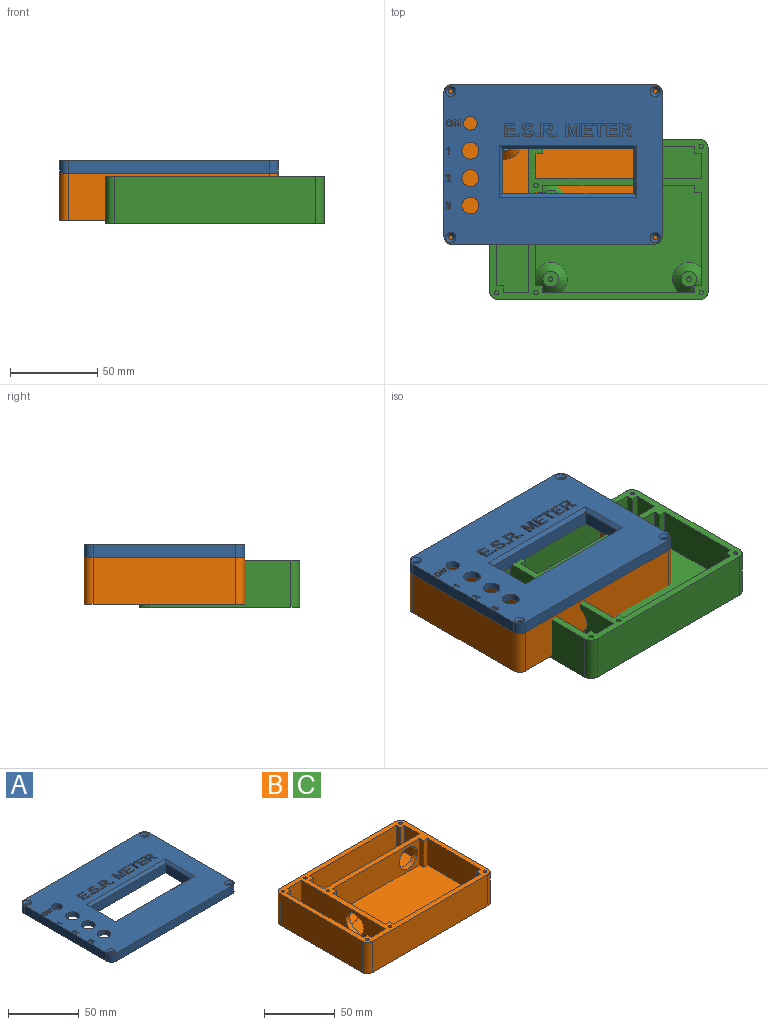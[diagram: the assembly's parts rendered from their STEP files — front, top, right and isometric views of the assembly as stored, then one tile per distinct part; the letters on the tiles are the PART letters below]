
ASSEMBLY  parts=3 mates=1
PART A: 312 faces, bbox 125.3x91.9x10 mm
  f0: plane 125.3x91.9mm, normal (0,0,1), area 8470.8mm2, adj f8,f9,f10,f11,f31,f32,f33,f34
  f1: plane 29.01x6mm, normal (-1,0,0), area 174.1mm2, adj f13,f43,f46,f47
  f2: plane 71.11x6mm, normal (0,1,0), area 426.7mm2, adj f13,f43,f44,f47
  f3: plane 71.44x6mm, normal (0,-1,0), area 428.6mm2, adj f13,f43,f45,f46
  f4: plane 27.36x6mm, normal (1,0,0), area 164.1mm2, adj f13,f43,f44,f45
  f5: plane 25.8x8mm, normal (1,0,0), area 206.4mm2, adj f6,f12,f42,f43
  f6: plane 74.8x8mm, normal (0,-1,0), area 598.4mm2, adj f5,f7,f40,f43
  f7: plane 25.8x8mm, normal (-1,0,0), area 206.4mm2, adj f6,f12,f39,f43
  f8: plane 81.9x7.1mm, normal (1,0,0), area 581.5mm2, adj f0,f26,f35,f38
  f9: plane 115.3x7.1mm, normal (0,1,0), area 818.6mm2, adj f0,f26,f35,f36
  f10: plane 81.9x7.1mm, normal (-1,0,0), area 581.5mm2, adj f0,f26,f36,f37
  f11: plane 115.3x7.1mm, normal (0,-1,0), area 818.6mm2, adj f0,f26,f37,f38
  f12: plane 74.8x8mm, normal (0,1,0), area 598.4mm2, adj f5,f7,f41,f43
  f13: plane 117.3x83.9mm, normal (0,0,-1), area 7111.6mm2, adj f1,f2,f3,f4,f14,f15,f16,f17
  f14: plane 4x3.1mm, normal (1,0,0), area 12.4mm2, adj f13,f15,f25,f26
  f15: plane 4x3.1mm, normal (0,-1,0), area 12.4mm2, adj f13,f14,f16,f26
  f16: plane 75.9x3.1mm, normal (1,0,0), area 235.3mm2, adj f13,f15,f17,f26
  f17: plane 4x3.1mm, normal (0,1,0), area 12.4mm2, adj f13,f16,f18,f26
  f18: plane 4x3.1mm, normal (1,0,0), area 12.4mm2, adj f13,f17,f19,f26
  f19: plane 109.3x3.1mm, normal (0,1,0), area 338.8mm2, adj f13,f18,f20,f26
  f20: plane 4x3.1mm, normal (-1,0,0), area 12.4mm2, adj f13,f19,f21,f26
  f21: plane 4x3.1mm, normal (0,1,0), area 12.4mm2, adj f13,f20,f22,f26
  f22: plane 75.9x3.1mm, normal (-1,0,0), area 235.3mm2, adj f13,f21,f23,f26
  f23: plane 4x3.1mm, normal (0,-1,0), area 12.4mm2, adj f13,f22,f24,f26
  f24: plane 4x3.1mm, normal (-1,0,0), area 12.4mm2, adj f13,f23,f25,f26
  f25: plane 109.3x3.1mm, normal (0,-1,0), area 338.8mm2, adj f13,f14,f24,f26
  f26: plane 125.3x91.9mm, normal (0,0,-1), area 1687.9mm2, adj f8,f9,f10,f11,f14,f15,f16,f17
  f27: cylinder r=1.5mm len=5.6mm, axis (0,0,1), area 52.8mm2, adj f26,f33
  f28: cylinder r=1.5mm len=5.6mm, axis (0,0,1), area 52.8mm2, adj f26,f32
  f29: cylinder r=1.5mm len=5.6mm, axis (0,0,1), area 52.8mm2, adj f26,f31
  f30: cylinder r=1.5mm len=5.6mm, axis (0,0,1), area 52.8mm2, adj f26,f34
  f31: cone r=1.5mm half-angle=45deg, axis (0,0,1), area 30mm2, adj f0,f29
  f32: cone r=1.5mm half-angle=45deg, axis (0,0,1), area 30mm2, adj f0,f28
  f33: cone r=1.5mm half-angle=45deg, axis (0,0,1), area 30mm2, adj f0,f27
  f34: cone r=1.5mm half-angle=45deg, axis (0,0,1), area 30mm2, adj f0,f30
  f35: cylinder r=5mm len=7.1mm, axis (0,0,1), area 55.8mm2, adj f0,f8,f9,f26
  f36: cylinder r=5mm len=7.1mm, axis (0,0,-1), area 55.8mm2, adj f0,f9,f10,f26
  f37: cylinder r=5mm len=7.1mm, axis (0,0,1), area 55.8mm2, adj f0,f10,f11,f26
  f38: cylinder r=5mm len=7.1mm, axis (0,0,-1), area 55.8mm2, adj f0,f8,f11,f26
  f39: plane 29.8x2mm, normal (-0.71,0,0.71), area 78.6mm2, adj f0,f7,f40,f41
  f40: plane 78.8x2mm, normal (0,-0.71,0.71), area 217.2mm2, adj f0,f6,f39,f42
  f41: plane 78.8x2mm, normal (0,0.71,0.71), area 217.2mm2, adj f0,f12,f39,f42
  f42: plane 29.8x2mm, normal (0.71,0,0.71), area 78.6mm2, adj f0,f5,f40,f41
  f43: plane 80.2x35.88mm, normal (0,0,-1), area 445.3mm2, adj f1,f2,f3,f4,f5,f6,f7,f12
  f44: cylinder r=2.3mm len=6mm, axis (0,0,1), area 60.5mm2, adj f2,f4,f13,f43
  f45: cylinder r=2.3mm len=6mm, axis (0,0,1), area 63.5mm2, adj f3,f4,f13,f43
  f46: cylinder r=2.3mm len=6mm, axis (0,0,1), area 56.6mm2, adj f1,f3,f13,f43
  f47: cylinder r=2.3mm len=6mm, axis (0,0,1), area 53.5mm2, adj f1,f2,f13,f43
  f48: cylinder r=1.3mm len=8mm, axis (0,0,-1), area 65.3mm2, adj f43,f49
  f49: plane 2.6x2.6mm, normal (0,0,-1), area 5.3mm2, adj f48
  f50: cylinder r=1.3mm len=8mm, axis (0,0,-1), area 65.3mm2, adj f43,f51
  f51: plane 2.6x2.6mm, normal (0,0,-1), area 5.3mm2, adj f50
  f52: cylinder r=1.3mm len=8mm, axis (0,0,-1), area 65.3mm2, adj f43,f53
  f53: plane 2.6x2.6mm, normal (0,0,-1), area 5.3mm2, adj f52
  f54: cylinder r=1.3mm len=8mm, axis (0,0,-1), area 65.3mm2, adj f43,f55
  f55: plane 2.6x2.6mm, normal (0,0,-1), area 5.3mm2, adj f54
  f56: cylinder r=4.85mm len=9.7mm, axis (0,0,1), area 121.9mm2, adj f0,f13
  f57: cylinder r=4.85mm len=9.7mm, axis (0,0,1), area 121.9mm2, adj f0,f13
  f58: cylinder r=4.85mm len=9.7mm, axis (0,0,1), area 121.9mm2, adj f0,f13
  f59: cylinder r=3.9mm len=7.8mm, axis (0,0,1), area 98mm2, adj f0,f13
  f60: plane 2x1.65mm, normal (-1,0,0), area 3.3mm2, adj f0,f61,f63,f64
  f61: plane 2x1.57mm, normal (0,-1,0), area 3.1mm2, adj f0,f60,f62,f64
  f62: plane 2x1.65mm, normal (1,0,0), area 3.3mm2, adj f0,f61,f63,f64
  f63: plane 2x1.57mm, normal (0,1,0), area 3.1mm2, adj f0,f60,f62,f64
  f64: plane 1.65x1.57mm, normal (0,0,1), area 2.6mm2, adj f60,f61,f62,f63
  f65: extruded ~2x1.02mm, area 2.2mm2, adj f66,f81,f83,f84
  f66: plane 2.09x2mm, normal (0,-1,0), area 4.2mm2, adj f65,f67,f83,f84
  f67: plane 2.26x2mm, normal (-1,0,0), area 4.5mm2, adj f66,f68,f83,f84
  f68: plane 2.05x2mm, normal (0,1,0), area 4.1mm2, adj f67,f69,f83,f84
  f69: extruded ~2x1.41mm, area 4.1mm2, adj f68,f81,f83,f84
  f70: plane 3.21x2.07mm, normal (-0.84,-0.54,0), area 7.6mm2, adj f0,f71,f82,f83
  f71: extruded ~2x1.23mm, area 3mm2, adj f0,f70,f72,f83
  f72: extruded ~2x1.39mm, area 3mm2, adj f0,f71,f73,f83
  f73: extruded ~2x1.69mm, area 3.8mm2, adj f0,f72,f74,f83
  f74: extruded ~2.11x2mm, area 4.5mm2, adj f0,f73,f75,f83
  f75: plane 3.82x2mm, normal (0,-1,0), area 7.6mm2, adj f0,f74,f76,f83
  f76: plane 7.64x2mm, normal (1,0,0), area 15.3mm2, adj f0,f75,f77,f83
  f77: plane 2x1.6mm, normal (0,1,0), area 3.2mm2, adj f0,f76,f78,f83
  f78: plane 2.9x2mm, normal (-1,0,0), area 5.8mm2, adj f0,f77,f79,f83
  f79: plane 2x1.88mm, normal (0,1,0), area 3.8mm2, adj f0,f78,f80,f83
  f80: plane 2.9x2mm, normal (0.85,0.52,0), area 6.8mm2, adj f0,f79,f82,f83
  f81: extruded ~2x0.85mm, area 1.9mm2, adj f65,f69,f83,f84
  f82: plane 2x1.8mm, normal (0,1,0), area 3.6mm2, adj f0,f70,f80,f83
  f83: plane 7.64x7.05mm, normal (0,0,1), area 31.6mm2, adj f65,f66,f67,f68,f69,f70,f71,f72
  f84: plane 3.46x2.26mm, normal (0,0,1), area 7.3mm2, adj f65,f66,f67,f68,f69,f81
  f85: extruded ~2x0.76mm, area 1.7mm2, adj f86,f97,f99,f100
  f86: extruded ~2x1.34mm, area 3.8mm2, adj f85,f87,f99,f100
  f87: extruded ~2x1.34mm, area 3.8mm2, adj f86,f88,f99,f100
  f88: extruded ~2x0.75mm, area 1.7mm2, adj f87,f89,f99,f100
  f89: extruded ~2x1mm, area 2.1mm2, adj f88,f97,f99,f100
  f90: extruded ~2x1.4mm, area 3.1mm2, adj f0,f91,f98,f99
  f91: extruded ~2x1.4mm, area 3.1mm2, adj f0,f90,f92,f99
  f92: extruded ~2x1.51mm, area 3.3mm2, adj f0,f91,f93,f99
  f93: extruded ~2x1.52mm, area 3.3mm2, adj f0,f92,f94,f99
  f94: extruded ~2x1.4mm, area 3.1mm2, adj f0,f93,f95,f99
  f95: extruded ~2x1.4mm, area 3.1mm2, adj f0,f94,f96,f99
  f96: extruded ~2x1.51mm, area 3.3mm2, adj f0,f95,f98,f99
  f97: extruded ~2x1mm, area 2.1mm2, adj f85,f89,f99,f100
  f98: extruded ~2x1.51mm, area 3.3mm2, adj f0,f90,f96,f99
  f99: plane 4.08x3.78mm, normal (0,0,1), area 8.2mm2, adj f85,f86,f87,f88,f89,f90,f91,f92
  f100: plane 2.68x2.01mm, normal (0,0,1), area 4.5mm2, adj f85,f86,f87,f88,f89,f97
  f101: plane 2x1.24mm, normal (-1,0,0), area 2.5mm2, adj f0,f102,f112,f113
  f102: plane 4.63x2mm, normal (0,-1,0), area 9.3mm2, adj f0,f101,f103,f113
  f103: plane 2.01x2mm, normal (-1,0,0), area 4mm2, adj f0,f102,f104,f113
  f104: plane 4.08x2mm, normal (0,1,0), area 8.2mm2, adj f0,f103,f105,f113
  f105: plane 2x1.24mm, normal (-1,0,0), area 2.5mm2, adj f0,f104,f106,f113
  f106: plane 4.08x2mm, normal (0,-1,0), area 8.2mm2, adj f0,f105,f107,f113
  f107: plane 2x1.92mm, normal (-1,0,0), area 3.8mm2, adj f0,f106,f108,f113
  f108: plane 4.41x2mm, normal (0,1,0), area 8.8mm2, adj f0,f107,f109,f113
  f109: plane 2x1.24mm, normal (-1,0,0), area 2.5mm2, adj f0,f108,f110,f113
  f110: plane 6.01x2mm, normal (0,-1,0), area 12mm2, adj f0,f109,f111,f113
  f111: plane 7.64x2mm, normal (1,0,0), area 15.3mm2, adj f0,f110,f112,f113
  f112: plane 6.23x2mm, normal (0,1,0), area 12.5mm2, adj f0,f101,f111,f113
  f113: plane 7.64x6.23mm, normal (0,0,1), area 28.5mm2, adj f101,f102,f103,f104,f105,f106,f107,f108
  f114: plane 2x1.24mm, normal (-1,0,0), area 2.5mm2, adj f0,f115,f125,f126
  f115: plane 4.63x2mm, normal (0,-1,0), area 9.3mm2, adj f0,f114,f116,f126
  f116: plane 2.01x2mm, normal (-1,0,0), area 4mm2, adj f0,f115,f117,f126
  f117: plane 4.08x2mm, normal (0,1,0), area 8.2mm2, adj f0,f116,f118,f126
  f118: plane 2x1.24mm, normal (-1,0,0), area 2.5mm2, adj f0,f117,f119,f126
  f119: plane 4.08x2mm, normal (0,-1,0), area 8.2mm2, adj f0,f118,f120,f126
  f120: plane 2x1.92mm, normal (-1,0,0), area 3.8mm2, adj f0,f119,f121,f126
  f121: plane 4.41x2mm, normal (0,1,0), area 8.8mm2, adj f0,f120,f122,f126
  f122: plane 2x1.24mm, normal (-1,0,0), area 2.5mm2, adj f0,f121,f123,f126
  f123: plane 6.01x2mm, normal (0,-1,0), area 12mm2, adj f0,f122,f124,f126
  f124: plane 7.64x2mm, normal (1,0,0), area 15.3mm2, adj f0,f123,f125,f126
  f125: plane 6.23x2mm, normal (0,1,0), area 12.5mm2, adj f0,f114,f124,f126
  f126: plane 7.64x6.23mm, normal (0,0,1), area 28.5mm2, adj f114,f115,f116,f117,f118,f119,f120,f121
  f127: plane 2x1.24mm, normal (-1,0,0), area 2.5mm2, adj f0,f128,f134,f135
  f128: plane 6.54x2mm, normal (0,-1,0), area 13.1mm2, adj f0,f127,f129,f135
  f129: plane 2x1.24mm, normal (1,0,0), area 2.5mm2, adj f0,f128,f130,f135
  f130: plane 2.47x2mm, normal (0,1,0), area 4.9mm2, adj f0,f129,f131,f135
  f131: plane 6.41x2mm, normal (1,0,0), area 12.8mm2, adj f0,f130,f132,f135
  f132: plane 2x1.6mm, normal (0,1,0), area 3.2mm2, adj f0,f131,f133,f135
  f133: plane 6.41x2mm, normal (-1,0,0), area 12.8mm2, adj f0,f132,f134,f135
  f134: plane 2.47x2mm, normal (0,1,0), area 4.9mm2, adj f0,f127,f133,f135
  f135: plane 7.64x6.54mm, normal (0,0,1), area 18.3mm2, adj f127,f128,f129,f130,f131,f132,f133,f134
  f136: plane 2x1.24mm, normal (-1,0,0), area 2.5mm2, adj f0,f137,f147,f148
  f137: plane 4.63x2mm, normal (0,-1,0), area 9.3mm2, adj f0,f136,f138,f148
  f138: plane 2.01x2mm, normal (-1,0,0), area 4mm2, adj f0,f137,f139,f148
  f139: plane 4.08x2mm, normal (0,1,0), area 8.2mm2, adj f0,f138,f140,f148
  f140: plane 2x1.24mm, normal (-1,0,0), area 2.5mm2, adj f0,f139,f141,f148
  f141: plane 4.08x2mm, normal (0,-1,0), area 8.2mm2, adj f0,f140,f142,f148
  f142: plane 2x1.92mm, normal (-1,0,0), area 3.8mm2, adj f0,f141,f143,f148
  f143: plane 4.41x2mm, normal (0,1,0), area 8.8mm2, adj f0,f142,f144,f148
  f144: plane 2x1.24mm, normal (-1,0,0), area 2.5mm2, adj f0,f143,f145,f148
  f145: plane 6.01x2mm, normal (0,-1,0), area 12mm2, adj f0,f144,f146,f148
  f146: plane 7.64x2mm, normal (1,0,0), area 15.3mm2, adj f0,f145,f147,f148
  f147: plane 6.23x2mm, normal (0,1,0), area 12.5mm2, adj f0,f136,f146,f148
  f148: plane 7.64x6.23mm, normal (0,0,1), area 28.5mm2, adj f136,f137,f138,f139,f140,f141,f142,f143
  f149: plane 2x0.76mm, normal (0,-1,0), area 1.5mm2, adj f0,f150,f162,f163
  f150: plane 2x1.88mm, normal (1,0,0), area 3.8mm2, adj f0,f149,f151,f163
  f151: extruded ~2x1.09mm, area 2.2mm2, adj f0,f150,f152,f163
  f152: plane 2x0.02mm, normal (0,-1,0), area 0mm2, adj f0,f151,f153,f163
  f153: plane 2.97x2mm, normal (-0.87,-0.5,0), area 6.9mm2, adj f0,f152,f154,f163
  f154: plane 2x1.06mm, normal (0,-1,0), area 2.1mm2, adj f0,f153,f155,f163
  f155: plane 3.97x2mm, normal (1,0,0), area 7.9mm2, adj f0,f154,f156,f163
  f156: plane 2x0.75mm, normal (0,1,0), area 1.5mm2, adj f0,f155,f157,f163
  f157: plane 2x1.87mm, normal (-1,0,0), area 3.7mm2, adj f0,f156,f158,f163
  f158: extruded ~2x1.13mm, area 2.3mm2, adj f0,f157,f159,f163
  f159: plane 2x0.02mm, normal (0,1,0), area 0mm2, adj f0,f158,f160,f163
  f160: plane 3x2mm, normal (0.87,0.5,0), area 6.9mm2, adj f0,f159,f161,f163
  f161: plane 2x1.07mm, normal (0,1,0), area 2.1mm2, adj f0,f160,f162,f163
  f162: plane 3.97x2mm, normal (-1,0,0), area 7.9mm2, adj f0,f149,f161,f163
  f163: plane 3.97x3.52mm, normal (0,0,1), area 8.9mm2, adj f149,f150,f151,f152,f153,f154,f155,f156
  f164: plane 7.64x2mm, normal (-1,0,0), area 15.3mm2, adj f0,f165,f184,f185
  f165: plane 2.13x2mm, normal (0,-1,0), area 4.3mm2, adj f0,f164,f166,f185
  f166: plane 4.49x2mm, normal (0.95,-0.3,0), area 9.4mm2, adj f0,f165,f167,f185
  f167: plane 2x1.23mm, normal (0.96,-0.27,0), area 2.5mm2, adj f0,f166,f168,f185
  f168: plane 2x1.02mm, normal (-0.97,-0.25,0), area 2.1mm2, adj f0,f167,f169,f185
  f169: plane 2x0.41mm, normal (-0.96,-0.28,0), area 0.9mm2, adj f0,f168,f170,f185
  f170: plane 4.27x2mm, normal (-0.95,-0.3,0), area 9mm2, adj f0,f169,f171,f185
  f171: plane 2.14x2mm, normal (0,-1,0), area 4.3mm2, adj f0,f170,f172,f185
  f172: plane 7.64x2mm, normal (1,0,0), area 15.3mm2, adj f0,f171,f173,f185
  f173: plane 2x1.42mm, normal (0,1,0), area 2.8mm2, adj f0,f172,f174,f185
  f174: plane 4.63x2mm, normal (-1,0,0), area 9.3mm2, adj f0,f173,f175,f185
  f175: extruded ~2x1.67mm, area 3.3mm2, adj f0,f174,f176,f185
  f176: plane 2.03x2mm, normal (0.96,0.27,0), area 4.2mm2, adj f0,f175,f177,f185
  f177: plane 4.26x2mm, normal (0.95,0.31,0), area 9mm2, adj f0,f176,f178,f185
  f178: plane 2x1.14mm, normal (0,1,0), area 2.3mm2, adj f0,f177,f179,f185
  f179: plane 4.26x2mm, normal (-0.95,0.31,0), area 9mm2, adj f0,f178,f180,f185
  f180: extruded ~2.03x2mm, area 4.2mm2, adj f0,f179,f181,f185
  f181: extruded ~2x1.35mm, area 2.7mm2, adj f0,f180,f182,f185
  f182: extruded ~2x0.31mm, area 0.6mm2, adj f0,f181,f183,f185
  f183: plane 4.63x2mm, normal (1,0,0), area 9.3mm2, adj f0,f182,f184,f185
  f184: plane 2x1.42mm, normal (0,1,0), area 2.8mm2, adj f0,f164,f183,f185
  f185: plane 7.77x7.64mm, normal (0,0,1), area 38.4mm2, adj f164,f165,f166,f167,f168,f169,f170,f171
  f186: plane 2x1.65mm, normal (-1,0,0), area 3.3mm2, adj f0,f187,f189,f190
  f187: plane 2x1.57mm, normal (0,-1,0), area 3.1mm2, adj f0,f186,f188,f190
  f188: plane 2x1.65mm, normal (1,0,0), area 3.3mm2, adj f0,f187,f189,f190
  f189: plane 2x1.57mm, normal (0,1,0), area 3.1mm2, adj f0,f186,f188,f190
  f190: plane 1.65x1.57mm, normal (0,0,1), area 2.6mm2, adj f186,f187,f188,f189
  f191: plane 2x1.65mm, normal (-1,0,0), area 3.3mm2, adj f0,f192,f194,f195
  f192: plane 2x1.57mm, normal (0,-1,0), area 3.1mm2, adj f0,f191,f193,f195
  f193: plane 2x1.65mm, normal (1,0,0), area 3.3mm2, adj f0,f192,f194,f195
  f194: plane 2x1.57mm, normal (0,1,0), area 3.1mm2, adj f0,f191,f193,f195
  f195: plane 1.65x1.57mm, normal (0,0,1), area 2.6mm2, adj f191,f192,f193,f194
  f196: extruded ~2x0.63mm, area 1.5mm2, adj f0,f197,f226,f227
  f197: extruded ~2x0.75mm, area 1.8mm2, adj f0,f196,f198,f227
  f198: extruded ~2x1.58mm, area 3.3mm2, adj f0,f197,f199,f227
  f199: extruded ~2x1.23mm, area 2.6mm2, adj f0,f198,f200,f227
  f200: extruded ~2x0.46mm, area 1.1mm2, adj f0,f199,f201,f227
  f201: extruded ~2x0.49mm, area 1mm2, adj f0,f200,f202,f227
  f202: extruded ~2x1.45mm, area 3.9mm2, adj f0,f201,f203,f227
  f203: extruded ~2x1.05mm, area 2.2mm2, adj f0,f202,f204,f227
  f204: extruded ~2x0.74mm, area 1.8mm2, adj f0,f203,f205,f227
  f205: plane 2x1.55mm, normal (-0.14,0.99,0), area 3.1mm2, adj f0,f204,f206,f227
  f206: extruded ~2x1.47mm, area 3.6mm2, adj f0,f205,f207,f227
  f207: extruded ~2.13x2mm, area 4.4mm2, adj f0,f206,f208,f227
  f208: extruded ~2.26x2mm, area 4.7mm2, adj f0,f207,f209,f227
  f209: extruded ~2x1.59mm, area 3.7mm2, adj f0,f208,f210,f227
  f210: extruded ~2x0.72mm, area 1.5mm2, adj f0,f209,f211,f227
  f211: extruded ~2x0.55mm, area 1.3mm2, adj f0,f210,f212,f227
  f212: extruded ~2x0.46mm, area 1.2mm2, adj f0,f211,f213,f227
  f213: extruded ~2x0.61mm, area 1.3mm2, adj f0,f212,f214,f227
  f214: extruded ~2x1.19mm, area 2.5mm2, adj f0,f213,f215,f227
  f215: extruded ~2x1.34mm, area 2.8mm2, adj f0,f214,f216,f227
  f216: extruded ~2x0.54mm, area 1.3mm2, adj f0,f215,f217,f227
  f217: extruded ~2x0.54mm, area 1.2mm2, adj f0,f216,f218,f227
  f218: extruded ~2x1.68mm, area 4.4mm2, adj f0,f217,f219,f227
  f219: extruded ~2x1.26mm, area 2.6mm2, adj f0,f218,f220,f227
  f220: extruded ~2x0.88mm, area 2.2mm2, adj f0,f219,f221,f227
  f221: plane 2x1.55mm, normal (0.16,-0.99,0), area 3.1mm2, adj f0,f220,f222,f227
  f222: extruded ~2x1.58mm, area 3.9mm2, adj f0,f221,f223,f227
  f223: extruded ~2.31x2mm, area 4.8mm2, adj f0,f222,f224,f227
  f224: extruded ~2.44x2mm, area 5.1mm2, adj f0,f223,f225,f227
  f225: extruded ~2x1.72mm, area 4mm2, adj f0,f224,f226,f227
  f226: extruded ~2x0.84mm, area 1.7mm2, adj f0,f196,f225,f227
  f227: plane 7.87x6.66mm, normal (0,0,1), area 26.8mm2, adj f196,f197,f198,f199,f200,f201,f202,f203
  f228: extruded ~2x1.02mm, area 2.2mm2, adj f229,f244,f246,f247
  f229: plane 2.09x2mm, normal (0,-1,0), area 4.2mm2, adj f228,f230,f246,f247
  f230: plane 2.26x2mm, normal (-1,0,0), area 4.5mm2, adj f229,f231,f246,f247
  f231: plane 2.05x2mm, normal (0,1,0), area 4.1mm2, adj f230,f232,f246,f247
  f232: extruded ~2x1.41mm, area 4.1mm2, adj f231,f244,f246,f247
  f233: plane 3.21x2.07mm, normal (-0.84,-0.54,0), area 7.6mm2, adj f0,f234,f245,f246
  f234: extruded ~2x1.23mm, area 3mm2, adj f0,f233,f235,f246
  f235: extruded ~2x1.39mm, area 3mm2, adj f0,f234,f236,f246
  f236: extruded ~2x1.69mm, area 3.8mm2, adj f0,f235,f237,f246
  f237: extruded ~2.11x2mm, area 4.5mm2, adj f0,f236,f238,f246
  f238: plane 3.82x2mm, normal (0,-1,0), area 7.6mm2, adj f0,f237,f239,f246
  f239: plane 7.64x2mm, normal (1,0,0), area 15.3mm2, adj f0,f238,f240,f246
  f240: plane 2x1.6mm, normal (0,1,0), area 3.2mm2, adj f0,f239,f241,f246
  f241: plane 2.9x2mm, normal (-1,0,0), area 5.8mm2, adj f0,f240,f242,f246
  f242: plane 2x1.88mm, normal (0,1,0), area 3.8mm2, adj f0,f241,f243,f246
  f243: plane 2.9x2mm, normal (0.85,0.52,0), area 6.8mm2, adj f0,f242,f245,f246
  f244: extruded ~2x0.85mm, area 1.9mm2, adj f228,f232,f246,f247
  f245: plane 2x1.8mm, normal (0,1,0), area 3.6mm2, adj f0,f233,f243,f246
  f246: plane 7.64x7.05mm, normal (0,0,1), area 31.6mm2, adj f228,f229,f230,f231,f232,f233,f234,f235
  f247: plane 3.46x2.26mm, normal (0,0,1), area 7.3mm2, adj f228,f229,f230,f231,f232,f244
  f248: plane 2x0.69mm, normal (0,-1,0), area 1.4mm2, adj f0,f249,f257,f258
  f249: plane 2x1.28mm, normal (0.62,-0.78,0), area 3.3mm2, adj f0,f248,f250,f258
  f250: plane 2x0.5mm, normal (0.78,0.63,0), area 1.3mm2, adj f0,f249,f251,f258
  f251: plane 2x0.46mm, normal (-0.63,0.78,0), area 1.2mm2, adj f0,f250,f252,f258
  f252: extruded ~2x0.29mm, area 0.8mm2, adj f0,f251,f253,f258
  f253: plane 2x0.41mm, normal (1,-0.03,0), area 0.8mm2, adj f0,f252,f254,f258
  f254: plane 2x0.38mm, normal (1,-0.02,0), area 0.8mm2, adj f0,f253,f255,f258
  f255: plane 2.3x2mm, normal (1,0,0), area 4.6mm2, adj f0,f254,f256,f258
  f256: plane 2x0.84mm, normal (0,1,0), area 1.7mm2, adj f0,f255,f257,f258
  f257: plane 3.97x2mm, normal (-1,0,0), area 7.9mm2, adj f0,f248,f256,f258
  f258: plane 3.97x1.97mm, normal (0,0,1), area 4.1mm2, adj f248,f249,f250,f251,f252,f253,f254,f255
  f259: plane 2x1.73mm, normal (0,-1,0), area 3.5mm2, adj f0,f260,f282,f283
  f260: plane 2x0.04mm, normal (-1,0,0), area 0.1mm2, adj f0,f259,f261,f283
  f261: plane 2x0.51mm, normal (-0.69,0.73,0), area 1.4mm2, adj f0,f260,f262,f283
  f262: extruded ~2x0.72mm, area 2mm2, adj f0,f261,f263,f283
  f263: extruded ~2x0.49mm, area 1.2mm2, adj f0,f262,f264,f283
  f264: extruded ~2x0.51mm, area 1.1mm2, adj f0,f263,f265,f283
  f265: extruded ~2x0.56mm, area 1.2mm2, adj f0,f264,f266,f283
  f266: extruded ~2x0.44mm, area 1.2mm2, adj f0,f265,f267,f283
  f267: extruded ~2x0.66mm, area 1.4mm2, adj f0,f266,f268,f283
  f268: extruded ~2x0.51mm, area 1mm2, adj f0,f267,f269,f283
  f269: extruded ~2x0.42mm, area 0.9mm2, adj f0,f268,f270,f283
  f270: extruded ~2x0.49mm, area 1.2mm2, adj f0,f269,f271,f283
  f271: plane 2x0.54mm, normal (0.76,0.65,0), area 1.4mm2, adj f0,f270,f272,f283
  f272: extruded ~2x0.45mm, area 1.1mm2, adj f0,f271,f273,f283
  f273: extruded ~2x0.45mm, area 0.9mm2, adj f0,f272,f274,f283
  f274: extruded ~2x0.35mm, area 0.8mm2, adj f0,f273,f275,f283
  f275: extruded ~2x0.36mm, area 0.8mm2, adj f0,f274,f276,f283
  f276: extruded ~2x0.31mm, area 0.6mm2, adj f0,f275,f277,f283
  f277: extruded ~2x0.32mm, area 0.8mm2, adj f0,f276,f278,f283
  f278: extruded ~2x0.63mm, area 1.7mm2, adj f0,f277,f279,f283
  f279: plane 2x1.01mm, normal (0.71,-0.7,0), area 2.8mm2, adj f0,f278,f280,f283
  f280: plane 2x0.58mm, normal (1,0,0), area 1.2mm2, adj f0,f279,f281,f283
  f281: plane 2.77x2mm, normal (0,1,0), area 5.5mm2, adj f0,f280,f282,f283
  f282: plane 2x0.71mm, normal (-1,0,0), area 1.4mm2, adj f0,f259,f281,f283
  f283: plane 4.02x2.78mm, normal (0,0,1), area 5.9mm2, adj f259,f260,f261,f262,f263,f264,f265,f266
  f284: extruded ~2x0.97mm, area 2mm2, adj f0,f285,f310,f311
  f285: extruded ~2x1.29mm, area 2.7mm2, adj f0,f284,f286,f311
  f286: plane 2x0.58mm, normal (0.83,0.56,0), area 1.4mm2, adj f0,f285,f287,f311
  f287: extruded ~2x0.45mm, area 1mm2, adj f0,f286,f288,f311
  f288: extruded ~2x0.4mm, area 0.8mm2, adj f0,f287,f289,f311
  f289: extruded ~2x0.56mm, area 1.7mm2, adj f0,f288,f290,f311
  f290: extruded ~2x0.41mm, area 1mm2, adj f0,f289,f291,f311
  f291: extruded ~2x0.67mm, area 1.4mm2, adj f0,f290,f292,f311
  f292: plane 2x0.31mm, normal (0,-1,0), area 0.6mm2, adj f0,f291,f293,f311
  f293: plane 2x0.64mm, normal (1,0,0), area 1.3mm2, adj f0,f292,f294,f311
  f294: plane 2x0.3mm, normal (0,1,0), area 0.6mm2, adj f0,f293,f295,f311
  f295: extruded ~2x0.73mm, area 1.5mm2, adj f0,f294,f296,f311
  f296: extruded ~2x0.4mm, area 1mm2, adj f0,f295,f297,f311
  f297: extruded ~2x0.45mm, area 1mm2, adj f0,f296,f298,f311
  f298: extruded ~2x0.61mm, area 1.3mm2, adj f0,f297,f299,f311
  f299: extruded ~2x0.55mm, area 1.1mm2, adj f0,f298,f300,f311
  f300: extruded ~2x0.51mm, area 1.1mm2, adj f0,f299,f301,f311
  f301: plane 2x0.71mm, normal (1,0,0), area 1.4mm2, adj f0,f300,f302,f311
  f302: extruded ~2x1.15mm, area 2.3mm2, adj f0,f301,f303,f311
  f303: extruded ~2x1.19mm, area 2.5mm2, adj f0,f302,f304,f311
  f304: extruded ~2x0.89mm, area 2mm2, adj f0,f303,f305,f311
  f305: extruded ~2x0.63mm, area 1.4mm2, adj f0,f304,f306,f311
  f306: extruded ~2x0.73mm, area 1.6mm2, adj f0,f305,f307,f311
  f307: plane 2x0.02mm, normal (-1,0,0), area 0mm2, adj f0,f306,f308,f311
  f308: extruded ~2x0.63mm, area 1.5mm2, adj f0,f307,f309,f311
  f309: extruded ~2x0.63mm, area 1.4mm2, adj f0,f308,f310,f311
  f310: extruded ~2x0.69mm, area 1.6mm2, adj f0,f284,f309,f311
  f311: plane 4.08x2.74mm, normal (0,0,1), area 5.9mm2, adj f284,f285,f286,f287,f288,f289,f290,f291
PART B: 72 faces, bbox 125.9x92.5x27.6 mm
  f0: plane 94.8x23mm, normal (0,1,0), area 1925.9mm2, adj f17,f32,f34,f35,f40
  f1: plane 83.9x23mm, normal (-1,0,0), area 1675.2mm2, adj f17,f41,f43,f49,f54
  f2: plane 115.3x27mm, normal (0,-1,0), area 3113.1mm2, adj f4,f17,f51,f53
  f3: plane 81.9x27mm, normal (1,0,0), area 2211.3mm2, adj f4,f17,f52,f53
  f4: plane 125.3x91.9mm, normal (0,0,-1), area 11493.6mm2, adj f2,f3,f31,f42,f50,f51,f52,f53
  f5: plane 23x4mm, normal (0,-1,0), area 92mm2, adj f6,f16,f17,f18
  f6: plane 53.6x23mm, normal (-1,0,0), area 1214.2mm2, adj f5,f7,f17,f18,f69
  f7: plane 21.47x4mm, normal (0,1,0), area 79.3mm2, adj f6,f8,f17,f69
  f8: plane 22.43x4.57mm, normal (-1,0,0), area 80.2mm2, adj f7,f9,f17,f69
  f9: plane 86.8x23mm, normal (0,1,0), area 1974mm2, adj f8,f10,f17,f18,f69,f70
  f10: plane 23.14x4.63mm, normal (1,0,0), area 83.5mm2, adj f9,f11,f17,f70
  f11: plane 23.34x4.53mm, normal (0,1,0), area 84.2mm2, adj f10,f12,f17,f70
  f12: plane 53.6x23mm, normal (1,0,0), area 967.4mm2, adj f11,f13,f17,f18,f54,f70,f71
  f13: plane 23.1x4.5mm, normal (0,-1,0), area 83.1mm2, adj f12,f14,f17,f71
  f14: plane 22.03x4mm, normal (1,0,0), area 81.8mm2, adj f13,f15,f17,f71
  f15: plane 86.8x23mm, normal (0,-1,0), area 1724.8mm2, adj f14,f16,f17,f18,f40,f71
  f16: plane 23x4mm, normal (-1,0,0), area 92mm2, adj f5,f15,f17,f18
  f17: plane 125.3x91.9mm, normal (0,0,1), area 2459mm2, adj f0,f1,f2,f3,f5,f6,f7,f8
  f18: plane 94.8x61.6mm, normal (0,0,1), area 5041.9mm2, adj f5,f6,f9,f12,f15,f16,f69,f70
  f19: cylinder r=4.5mm len=9mm, axis (0,0,-1), area 14.1mm2, adj f20,f71
  f20: plane 9x9mm, normal (0,0,1), area 58.7mm2, adj f19,f29
  f21: cylinder r=4.5mm len=9mm, axis (0,0,-1), area 14.1mm2, adj f22,f70
  f22: plane 9x9mm, normal (0,0,1), area 58.7mm2, adj f21,f27
  f23: cylinder r=4.5mm len=9mm, axis (0,0,-1), area 14.1mm2, adj f24,f69
  f24: plane 9x9mm, normal (0,0,1), area 58.7mm2, adj f23,f25
  f25: cylinder r=1.25mm len=8mm, axis (0,0,1), area 62.8mm2, adj f24,f26
  f26: plane 2.5x2.5mm, normal (0,0,1), area 4.9mm2, adj f25
  f27: cylinder r=1.25mm len=8mm, axis (0,0,1), area 62.8mm2, adj f22,f28
  f28: plane 2.5x2.5mm, normal (0,0,1), area 4.9mm2, adj f27
  f29: cylinder r=1.25mm len=8mm, axis (0,0,1), area 62.8mm2, adj f20,f30
  f30: plane 2.5x2.5mm, normal (0,0,1), area 4.9mm2, adj f29
  f31: plane 115.3x27mm, normal (0,1,0), area 3113.1mm2, adj f4,f17,f50,f52
  f32: plane 94.8x18.3mm, normal (0,0,1), area 1702.8mm2, adj f0,f33,f34,f35,f36,f37,f38,f39
  f33: plane 23x4mm, normal (0,-1,0), area 92mm2, adj f17,f32,f34,f39
  f34: plane 23x14.3mm, normal (-1,0,0), area 328.9mm2, adj f0,f17,f32,f33
  f35: plane 23x14.3mm, normal (1,0,0), area 328.9mm2, adj f0,f17,f32,f36
  f36: plane 23x4mm, normal (0,-1,0), area 92mm2, adj f17,f32,f35,f37
  f37: plane 23x4mm, normal (1,0,0), area 92mm2, adj f17,f32,f36,f38
  f38: plane 86.8x23mm, normal (0,-1,0), area 1996.4mm2, adj f17,f32,f37,f39
  f39: plane 23x4mm, normal (-1,0,0), area 92mm2, adj f17,f32,f33,f38
  f40: cylinder r=9mm len=18mm, axis (0,-1,0), area 226.2mm2, adj f0,f15
  f41: plane 23x14.5mm, normal (0,-1,0), area 333.5mm2, adj f1,f17,f48,f49
  f42: plane 81.9x27mm, normal (-1,0,0), area 2211.3mm2, adj f4,f17,f50,f51
  f43: plane 23x14.5mm, normal (0,1,0), area 333.5mm2, adj f1,f17,f44,f49
  f44: plane 23x4mm, normal (1,0,0), area 92mm2, adj f17,f43,f45,f49
  f45: plane 23x4mm, normal (0,1,0), area 92mm2, adj f17,f44,f46,f49
  f46: plane 76.31x23mm, normal (1,0,0), area 1755mm2, adj f17,f45,f47,f49
  f47: plane 23x4mm, normal (0,-1,0), area 92mm2, adj f17,f46,f48,f49
  f48: plane 23x3.59mm, normal (1,0,0), area 82.7mm2, adj f17,f41,f47,f49
  f49: plane 83.9x18.5mm, normal (0,0,1), area 1521.8mm2, adj f1,f41,f43,f44,f45,f46,f47,f48
  f50: cylinder r=5mm len=27mm, axis (0,0,1), area 212.1mm2, adj f4,f17,f31,f42
  f51: cylinder r=5mm len=27mm, axis (0,0,1), area 212.1mm2, adj f2,f4,f17,f42
  f52: cylinder r=5mm len=27mm, axis (0,0,1), area 212.1mm2, adj f3,f4,f17,f31
  f53: cylinder r=5mm len=27mm, axis (0,0,1), area 212.1mm2, adj f2,f3,f4,f17
  f54: cylinder r=9mm len=18mm, axis (1,0,0), area 226.2mm2, adj f1,f12
  f55: cylinder r=1.25mm len=10mm, axis (0,0,1), area 78.5mm2, adj f17,f56
  f56: plane 2.5x2.5mm, normal (0,0,1), area 4.9mm2, adj f55
  f57: cylinder r=1.25mm len=10mm, axis (0,0,1), area 78.5mm2, adj f17,f58
  f58: plane 2.5x2.5mm, normal (0,0,1), area 4.9mm2, adj f57
  f59: cylinder r=1.25mm len=10mm, axis (0,0,1), area 78.5mm2, adj f17,f60
  f60: plane 2.5x2.5mm, normal (0,0,1), area 4.9mm2, adj f59
  f61: cylinder r=1.25mm len=10mm, axis (0,0,1), area 78.5mm2, adj f17,f62
  f62: plane 2.5x2.5mm, normal (0,0,1), area 4.9mm2, adj f61
  f63: cylinder r=1.25mm len=10mm, axis (0,0,1), area 78.5mm2, adj f17,f64
  f64: plane 2.5x2.5mm, normal (0,0,1), area 4.9mm2, adj f63
  f65: cylinder r=1.25mm len=10mm, axis (0,0,1), area 78.5mm2, adj f17,f66
  f66: plane 2.5x2.5mm, normal (0,0,1), area 4.9mm2, adj f65
  f67: cylinder r=1.25mm len=10mm, axis (0,0,1), area 78.5mm2, adj f17,f68
  f68: plane 2.5x2.5mm, normal (0,0,1), area 4.9mm2, adj f67
  f69: cone r=4.5mm half-angle=45deg, axis (0,0,-1), area 241.9mm2, adj f6,f7,f8,f9,f18,f23
  f70: cone r=4.5mm half-angle=45deg, axis (0,0,-1), area 271mm2, adj f9,f10,f11,f12,f18,f21
  f71: cone r=4.5mm half-angle=45deg, axis (0,0,-1), area 258.7mm2, adj f12,f13,f14,f15,f18,f19
PART C: same geometry as B
PLACE A t=(13.81,7.94,31.91)mm
PLACE B t=(-26.34,31.59,1.81)mm
PLACE C at identity
MATE slider B.f63 <-> A.f27  axis (0,0,1) through (-44.84,-34.01,28.81)mm
